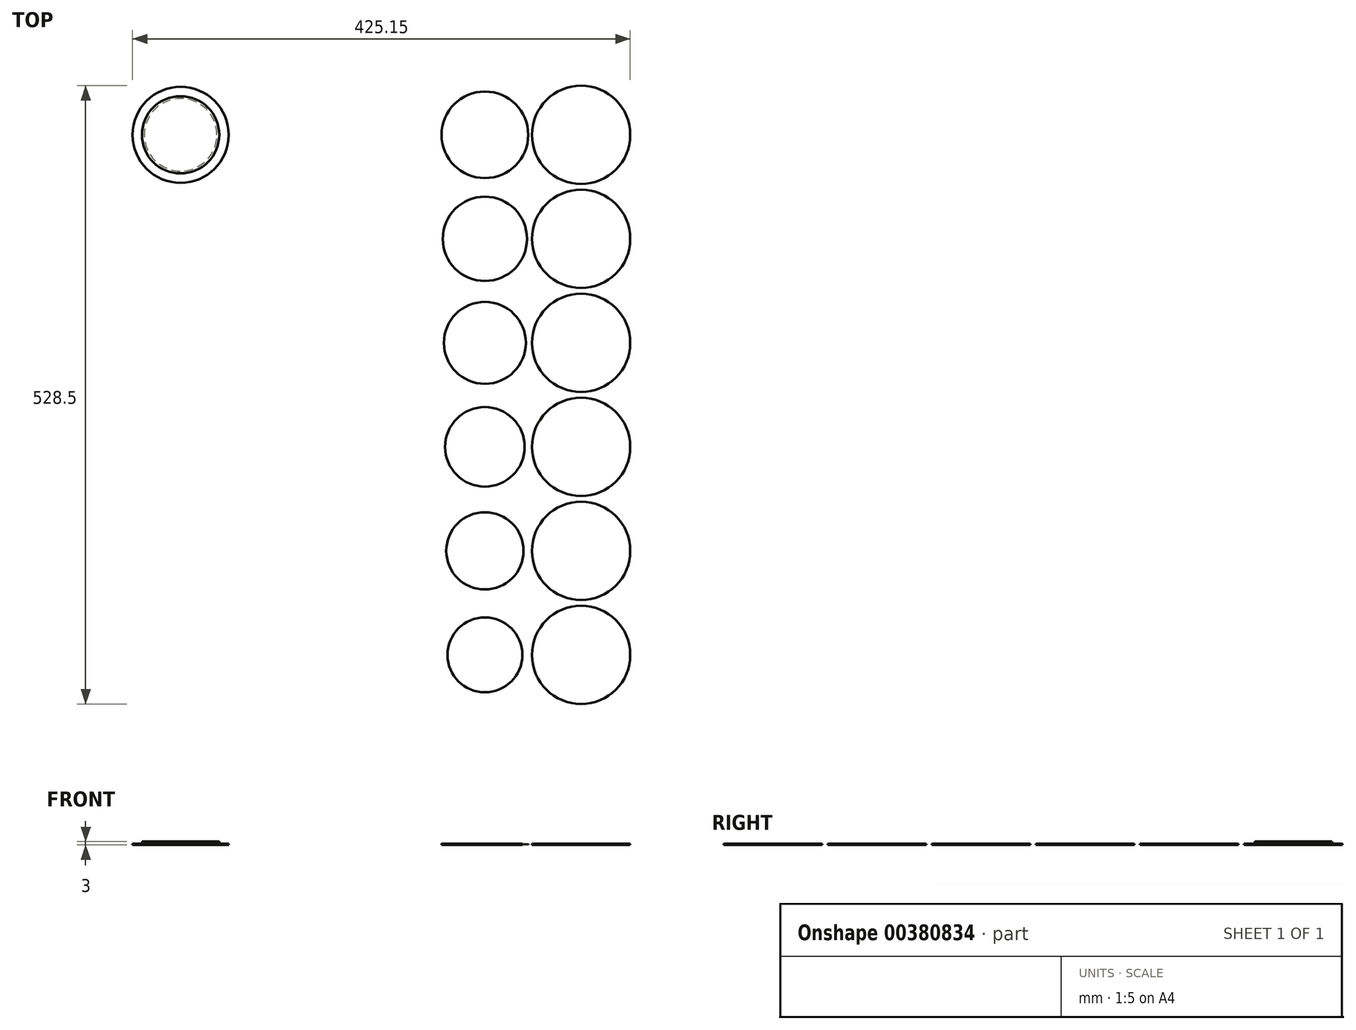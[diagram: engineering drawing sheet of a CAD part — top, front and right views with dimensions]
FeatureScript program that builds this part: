
annotation { "Feature Type Name" : "Feature", "Feature Type Description" : "" }
export const myFeature = defineFeature(function(context is Context, id is Id, definition is map)
    precondition{}
    {
        {
            var Q0;
            Q0=qCreatedBy(makeId("Top.planeOp"),FACE);
            var sketch = newSketch(context, id + "F0", { "sketchPlane" : qUnion([Q0])});
            skArc(sketch, "E0", {"start": v(2.5, -41.93) * mm, "mid": v(0, 42) * mm, "end": v(-2.5, -41.93) * mm});
            skArc(sketch, "E1", {"start": v(2.5, -36.92) * mm, "mid": v(0, 37) * mm, "end": v(-2.5, -36.92) * mm});
            skArc(sketch, "E2", {"start": v(92.4, -41.85) * mm, "mid": v(88.9, 42) * mm, "end": v(85.4, -41.85) * mm});
            skArc(sketch, "E3", {"start": v(92.4, -36.83) * mm, "mid": v(88.9, 37) * mm, "end": v(85.4, -36.83) * mm});
            skArc(sketch, "E4", {"start": v(182.3, -41.76) * mm, "mid": v(177.8, 42) * mm, "end": v(173.3, -41.76) * mm});
            skArc(sketch, "E5", {"start": v(182.3, -36.73) * mm, "mid": v(177.8, 37) * mm, "end": v(173.3, -36.73) * mm});
            skLineSegment(sketch, "E6", {"start": v(0, 0) * mm, "end": v(88.9, 0) * mm, "construction": true});
            skLineSegment(sketch, "E7", {"start": v(88.9, 0) * mm, "end": v(177.8, 0) * mm, "construction": true});
            skLineSegment(sketch, "E8", {"start": v(0, 0) * mm, "end": v(0, -42) * mm, "construction": true});
            skLineSegment(sketch, "E9", {"start": v(-2.5, -36.92) * mm, "end": v(-2.5, -41.93) * mm});
            skLineSegment(sketch, "E10", {"start": v(2.5, -36.92) * mm, "end": v(2.5, -41.93) * mm});
            skLineSegment(sketch, "E11", {"start": v(88.9, 0) * mm, "end": v(88.9, -42) * mm, "construction": true});
            skLineSegment(sketch, "E12", {"start": v(177.8, 0) * mm, "end": v(177.8, -42) * mm, "construction": true});
            skLineSegment(sketch, "E13", {"start": v(85.4, -36.83) * mm, "end": v(85.4, -41.85) * mm});
            skLineSegment(sketch, "E14", {"start": v(92.4, -36.83) * mm, "end": v(92.4, -41.85) * mm});
            skLineSegment(sketch, "E15", {"start": v(173.3, -36.73) * mm, "end": v(173.3, -41.76) * mm});
            skLineSegment(sketch, "E16", {"start": v(182.3, -36.73) * mm, "end": v(182.3, -41.76) * mm});
            skLineSegment(sketch, "E17.0.1.0", {"start": v(0, -88.9) * mm, "end": v(88.9, -88.9) * mm, "construction": true});
            skLineSegment(sketch, "E17.0.1.1", {"start": v(0, -88.9) * mm, "end": v(0, -130.9) * mm, "construction": true});
            skLineSegment(sketch, "E17.0.1.2", {"start": v(88.9, -88.9) * mm, "end": v(88.9, -130.9) * mm, "construction": true});
            skLineSegment(sketch, "E17.0.1.3", {"start": v(88.9, -88.9) * mm, "end": v(177.8, -88.9) * mm, "construction": true});
            skCircle(sketch, "E17.0.1.4", {"center": v(88.9, -88.9) * mm, "radius": 37 * mm, "construction": true});
            skLineSegment(sketch, "E17.0.1.5", {"start": v(177.8, -88.9) * mm, "end": v(177.8, -130.9) * mm, "construction": true});
            skArc(sketch, "E17.0.1.6", {"start": v(92.4, -130.75) * mm, "mid": v(88.9, -46.9) * mm, "end": v(85.4, -130.75) * mm});
            skCircle(sketch, "E17.0.1.7", {"center": v(177.8, -88.9) * mm, "radius": 37 * mm, "construction": true});
            skArc(sketch, "E17.0.1.8", {"start": v(182.3, -130.66) * mm, "mid": v(177.8, -46.9) * mm, "end": v(173.3, -130.66) * mm});
            skCircle(sketch, "E17.0.1.9", {"center": v(0, -88.9) * mm, "radius": 37 * mm, "construction": true});
            skArc(sketch, "E17.0.1.10", {"start": v(2.5, -130.83) * mm, "mid": v(0, -46.9) * mm, "end": v(-2.5, -130.83) * mm});
            skLineSegment(sketch, "E17.0.1.11", {"start": v(92.4, -124.73) * mm, "end": v(92.4, -130.75) * mm});
            skLineSegment(sketch, "E17.0.1.12", {"start": v(85.4, -124.73) * mm, "end": v(85.4, -130.75) * mm});
            skLineSegment(sketch, "E17.0.1.13", {"start": v(2.5, -124.81) * mm, "end": v(2.5, -130.83) * mm});
            skLineSegment(sketch, "E17.0.1.14", {"start": v(173.3, -124.62) * mm, "end": v(173.3, -130.66) * mm});
            skLineSegment(sketch, "E17.0.1.15", {"start": v(182.3, -124.62) * mm, "end": v(182.3, -130.66) * mm});
            skLineSegment(sketch, "E17.0.1.16", {"start": v(-2.5, -125.82) * mm, "end": v(-2.5, -130.83) * mm});
            skLineSegment(sketch, "E17.0.2.0", {"start": v(0, -177.8) * mm, "end": v(88.9, -177.8) * mm, "construction": true});
            skLineSegment(sketch, "E17.0.2.1", {"start": v(0, -177.8) * mm, "end": v(0, -219.8) * mm, "construction": true});
            skLineSegment(sketch, "E17.0.2.2", {"start": v(88.9, -177.8) * mm, "end": v(88.9, -219.8) * mm, "construction": true});
            skLineSegment(sketch, "E17.0.2.3", {"start": v(88.9, -177.8) * mm, "end": v(177.8, -177.8) * mm, "construction": true});
            skCircle(sketch, "E17.0.2.4", {"center": v(88.9, -177.8) * mm, "radius": 37 * mm, "construction": true});
            skLineSegment(sketch, "E17.0.2.5", {"start": v(177.8, -177.8) * mm, "end": v(177.8, -219.8) * mm, "construction": true});
            skArc(sketch, "E17.0.2.6", {"start": v(92.4, -219.65) * mm, "mid": v(88.9, -135.8) * mm, "end": v(85.4, -219.65) * mm});
            skCircle(sketch, "E17.0.2.7", {"center": v(177.8, -177.8) * mm, "radius": 37 * mm, "construction": true});
            skArc(sketch, "E17.0.2.8", {"start": v(182.3, -219.56) * mm, "mid": v(177.8, -135.8) * mm, "end": v(173.3, -219.56) * mm});
            skCircle(sketch, "E17.0.2.9", {"center": v(0, -177.8) * mm, "radius": 37 * mm, "construction": true});
            skArc(sketch, "E17.0.2.10", {"start": v(2.5, -219.73) * mm, "mid": v(0, -135.8) * mm, "end": v(-2.5, -219.73) * mm});
            skLineSegment(sketch, "E17.0.2.11", {"start": v(92.4, -212.62) * mm, "end": v(92.4, -219.65) * mm});
            skLineSegment(sketch, "E17.0.2.12", {"start": v(85.4, -212.62) * mm, "end": v(85.4, -219.65) * mm});
            skLineSegment(sketch, "E17.0.2.13", {"start": v(2.5, -212.71) * mm, "end": v(2.5, -219.73) * mm});
            skLineSegment(sketch, "E17.0.2.14", {"start": v(173.3, -212.5) * mm, "end": v(173.3, -219.56) * mm});
            skLineSegment(sketch, "E17.0.2.15", {"start": v(182.3, -212.5) * mm, "end": v(182.3, -219.56) * mm});
            skLineSegment(sketch, "E17.0.2.16", {"start": v(-2.5, -212.71) * mm, "end": v(-2.5, -219.73) * mm});
            skLineSegment(sketch, "E17.0.3.0", {"start": v(0, -266.7) * mm, "end": v(88.9, -266.7) * mm, "construction": true});
            skLineSegment(sketch, "E17.0.3.1", {"start": v(0, -266.7) * mm, "end": v(0, -308.7) * mm, "construction": true});
            skLineSegment(sketch, "E17.0.3.2", {"start": v(88.9, -266.7) * mm, "end": v(88.9, -308.7) * mm, "construction": true});
            skLineSegment(sketch, "E17.0.3.3", {"start": v(88.9, -266.7) * mm, "end": v(177.8, -266.7) * mm, "construction": true});
            skCircle(sketch, "E17.0.3.4", {"center": v(88.9, -266.7) * mm, "radius": 37 * mm, "construction": true});
            skLineSegment(sketch, "E17.0.3.5", {"start": v(177.8, -266.7) * mm, "end": v(177.8, -308.7) * mm, "construction": true});
            skArc(sketch, "E17.0.3.6", {"start": v(92.4, -308.55) * mm, "mid": v(88.9, -224.7) * mm, "end": v(85.4, -308.55) * mm});
            skCircle(sketch, "E17.0.3.7", {"center": v(177.8, -266.7) * mm, "radius": 37 * mm, "construction": true});
            skArc(sketch, "E17.0.3.8", {"start": v(182.3, -308.46) * mm, "mid": v(177.8, -224.7) * mm, "end": v(173.3, -308.46) * mm});
            skCircle(sketch, "E17.0.3.9", {"center": v(0, -266.7) * mm, "radius": 37 * mm, "construction": true});
            skArc(sketch, "E17.0.3.10", {"start": v(2.5, -308.63) * mm, "mid": v(0, -224.7) * mm, "end": v(-2.5, -308.63) * mm});
            skLineSegment(sketch, "E17.0.3.11", {"start": v(92.4, -300.52) * mm, "end": v(92.4, -308.55) * mm});
            skLineSegment(sketch, "E17.0.3.12", {"start": v(85.4, -300.52) * mm, "end": v(85.4, -308.55) * mm});
            skLineSegment(sketch, "E17.0.3.13", {"start": v(2.5, -300.6) * mm, "end": v(2.5, -308.63) * mm});
            skLineSegment(sketch, "E17.0.3.14", {"start": v(173.3, -300.4) * mm, "end": v(173.3, -308.46) * mm});
            skLineSegment(sketch, "E17.0.3.15", {"start": v(182.3, -300.4) * mm, "end": v(182.3, -308.46) * mm});
            skLineSegment(sketch, "E17.0.3.16", {"start": v(-2.5, -300.6) * mm, "end": v(-2.5, -308.63) * mm});
            skLineSegment(sketch, "E17.0.4.0", {"start": v(0, -355.6) * mm, "end": v(88.9, -355.6) * mm, "construction": true});
            skLineSegment(sketch, "E17.0.4.1", {"start": v(0, -355.6) * mm, "end": v(0, -397.6) * mm, "construction": true});
            skLineSegment(sketch, "E17.0.4.2", {"start": v(88.9, -355.6) * mm, "end": v(88.9, -397.6) * mm, "construction": true});
            skLineSegment(sketch, "E17.0.4.3", {"start": v(88.9, -355.6) * mm, "end": v(177.8, -355.6) * mm, "construction": true});
            skCircle(sketch, "E17.0.4.4", {"center": v(88.9, -355.6) * mm, "radius": 37 * mm, "construction": true});
            skLineSegment(sketch, "E17.0.4.5", {"start": v(177.8, -355.6) * mm, "end": v(177.8, -397.6) * mm, "construction": true});
            skArc(sketch, "E17.0.4.6", {"start": v(92.4, -397.45) * mm, "mid": v(88.9, -313.6) * mm, "end": v(85.4, -397.45) * mm});
            skCircle(sketch, "E17.0.4.7", {"center": v(177.8, -355.6) * mm, "radius": 37 * mm, "construction": true});
            skArc(sketch, "E17.0.4.8", {"start": v(182.3, -397.36) * mm, "mid": v(177.8, -313.6) * mm, "end": v(173.3, -397.36) * mm});
            skCircle(sketch, "E17.0.4.9", {"center": v(0, -355.6) * mm, "radius": 37 * mm, "construction": true});
            skArc(sketch, "E17.0.4.10", {"start": v(2.5, -397.53) * mm, "mid": v(0, -313.6) * mm, "end": v(-2.5, -397.53) * mm});
            skLineSegment(sketch, "E17.0.4.11", {"start": v(92.4, -388.41) * mm, "end": v(92.4, -397.45) * mm});
            skLineSegment(sketch, "E17.0.4.12", {"start": v(85.4, -388.41) * mm, "end": v(85.4, -397.45) * mm});
            skLineSegment(sketch, "E17.0.4.13", {"start": v(2.5, -388.5) * mm, "end": v(2.5, -397.53) * mm});
            skLineSegment(sketch, "E17.0.4.14", {"start": v(173.3, -388.3) * mm, "end": v(173.3, -397.36) * mm});
            skLineSegment(sketch, "E17.0.4.15", {"start": v(182.3, -388.3) * mm, "end": v(182.3, -397.36) * mm});
            skLineSegment(sketch, "E17.0.4.16", {"start": v(-2.5, -388.5) * mm, "end": v(-2.5, -397.53) * mm});
            skLineSegment(sketch, "E17.0.5.0", {"start": v(0, -444.5) * mm, "end": v(88.9, -444.5) * mm, "construction": true});
            skLineSegment(sketch, "E17.0.5.1", {"start": v(0, -444.5) * mm, "end": v(0, -486.5) * mm, "construction": true});
            skLineSegment(sketch, "E17.0.5.2", {"start": v(88.9, -444.5) * mm, "end": v(88.9, -486.5) * mm, "construction": true});
            skLineSegment(sketch, "E17.0.5.3", {"start": v(88.9, -444.5) * mm, "end": v(177.8, -444.5) * mm, "construction": true});
            skCircle(sketch, "E17.0.5.4", {"center": v(88.9, -444.5) * mm, "radius": 37 * mm, "construction": true});
            skLineSegment(sketch, "E17.0.5.5", {"start": v(177.8, -444.5) * mm, "end": v(177.8, -486.5) * mm, "construction": true});
            skArc(sketch, "E17.0.5.6", {"start": v(92.4, -486.35) * mm, "mid": v(88.9, -402.5) * mm, "end": v(85.4, -486.35) * mm});
            skCircle(sketch, "E17.0.5.7", {"center": v(177.8, -444.5) * mm, "radius": 37 * mm, "construction": true});
            skArc(sketch, "E17.0.5.8", {"start": v(182.3, -486.26) * mm, "mid": v(177.8, -402.5) * mm, "end": v(173.3, -486.26) * mm});
            skCircle(sketch, "E17.0.5.9", {"center": v(0, -444.5) * mm, "radius": 37 * mm, "construction": true});
            skArc(sketch, "E17.0.5.10", {"start": v(2.5, -486.43) * mm, "mid": v(0, -402.5) * mm, "end": v(-2.5, -486.43) * mm});
            skLineSegment(sketch, "E17.0.5.11", {"start": v(92.4, -476.3) * mm, "end": v(92.4, -486.35) * mm});
            skLineSegment(sketch, "E17.0.5.12", {"start": v(85.4, -476.3) * mm, "end": v(85.4, -486.35) * mm});
            skLineSegment(sketch, "E17.0.5.13", {"start": v(2.5, -476.4) * mm, "end": v(2.5, -486.43) * mm});
            skLineSegment(sketch, "E17.0.5.14", {"start": v(173.3, -476.18) * mm, "end": v(173.3, -486.26) * mm});
            skLineSegment(sketch, "E17.0.5.15", {"start": v(182.3, -476.18) * mm, "end": v(182.3, -486.26) * mm});
            skLineSegment(sketch, "E17.0.5.16", {"start": v(-2.5, -476.4) * mm, "end": v(-2.5, -486.43) * mm});
            skLineSegment(sketch, "E17.direction1", {"start": v(2.5, -41.93) * mm, "end": v(22.9, -41.93) * mm, "construction": true});
            skLineSegment(sketch, "E17.direction2", {"start": v(-2.5, -41.93) * mm, "end": v(-2.5, -130.83) * mm, "construction": true});
            skArc(sketch, "E18", {"start": v(2.5, -124.81) * mm, "mid": v(0, -52.9) * mm, "end": v(-2.5, -124.81) * mm});
            skArc(sketch, "E19", {"start": v(92.4, -124.73) * mm, "mid": v(88.9, -52.9) * mm, "end": v(85.4, -124.73) * mm});
            skArc(sketch, "E20", {"start": v(182.3, -124.62) * mm, "mid": v(177.8, -52.9) * mm, "end": v(173.3, -124.62) * mm});
            skArc(sketch, "E21", {"start": v(182.3, -212.5) * mm, "mid": v(177.8, -142.8) * mm, "end": v(173.3, -212.5) * mm});
            skArc(sketch, "E22", {"start": v(92.4, -212.62) * mm, "mid": v(88.9, -142.8) * mm, "end": v(85.4, -212.62) * mm});
            skArc(sketch, "E23", {"start": v(2.5, -212.71) * mm, "mid": v(0, -142.8) * mm, "end": v(-2.5, -212.71) * mm});
            skArc(sketch, "E24", {"start": v(2.5, -300.6) * mm, "mid": v(0, -232.7) * mm, "end": v(-2.5, -300.6) * mm});
            skArc(sketch, "E25", {"start": v(92.4, -300.52) * mm, "mid": v(88.9, -232.7) * mm, "end": v(85.4, -300.52) * mm});
            skArc(sketch, "E26", {"start": v(182.3, -300.4) * mm, "mid": v(177.8, -232.7) * mm, "end": v(173.3, -300.4) * mm});
            skArc(sketch, "E27", {"start": v(182.3, -388.3) * mm, "mid": v(177.8, -322.6) * mm, "end": v(173.3, -388.3) * mm});
            skArc(sketch, "E28", {"start": v(92.4, -388.41) * mm, "mid": v(88.9, -322.6) * mm, "end": v(85.4, -388.41) * mm});
            skArc(sketch, "E29", {"start": v(2.5, -388.5) * mm, "mid": v(0, -322.6) * mm, "end": v(-2.5, -388.5) * mm});
            skArc(sketch, "E30", {"start": v(2.5, -476.4) * mm, "mid": v(0, -412.5) * mm, "end": v(-2.5, -476.4) * mm});
            skArc(sketch, "E31", {"start": v(92.4, -476.3) * mm, "mid": v(88.9, -412.5) * mm, "end": v(85.4, -476.3) * mm});
            skArc(sketch, "E32", {"start": v(182.3, -476.18) * mm, "mid": v(177.8, -412.5) * mm, "end": v(173.3, -476.18) * mm});
            skPoint(sketch, "E33.orphan", {"position": v(2.5, -125.82) * mm});
            skLineSegment(sketch, "E34", {"start": v(-2.5, -125.82) * mm, "end": v(-2.5, -124.81) * mm});
            skPoint(sketch, "E35.orphan", {"position": v(85.4, -125.73) * mm});
            skPoint(sketch, "E36.orphan", {"position": v(92.4, -125.73) * mm});
            skPoint(sketch, "E37.orphan", {"position": v(173.3, -125.63) * mm});
            skPoint(sketch, "E38.orphan", {"position": v(182.3, -125.63) * mm});
            skPoint(sketch, "E39.orphan", {"position": v(-2.5, -214.72) * mm});
            skPoint(sketch, "E40.orphan", {"position": v(2.5, -214.72) * mm});
            skPoint(sketch, "E41.orphan", {"position": v(85.4, -214.63) * mm});
            skPoint(sketch, "E42.orphan", {"position": v(92.4, -214.63) * mm});
            skPoint(sketch, "E43.orphan", {"position": v(173.3, -214.53) * mm});
            skPoint(sketch, "E44.orphan", {"position": v(182.3, -214.53) * mm});
            skPoint(sketch, "E45.orphan", {"position": v(182.3, -303.43) * mm});
            skPoint(sketch, "E46.orphan", {"position": v(173.3, -303.43) * mm});
            skPoint(sketch, "E47.orphan", {"position": v(92.4, -303.53) * mm});
            skPoint(sketch, "E48.orphan", {"position": v(85.4, -303.53) * mm});
            skPoint(sketch, "E49.orphan", {"position": v(-2.5, -303.62) * mm});
            skPoint(sketch, "E50.orphan", {"position": v(2.5, -303.62) * mm});
            skPoint(sketch, "E51.orphan", {"position": v(-2.5, -392.52) * mm});
            skPoint(sketch, "E52.orphan", {"position": v(2.5, -392.52) * mm});
            skPoint(sketch, "E53.orphan", {"position": v(85.4, -392.43) * mm});
            skPoint(sketch, "E54.orphan", {"position": v(92.4, -392.43) * mm});
            skPoint(sketch, "E55.orphan", {"position": v(182.3, -392.33) * mm});
            skPoint(sketch, "E56.orphan", {"position": v(173.3, -392.33) * mm});
            skPoint(sketch, "E57.orphan", {"position": v(-2.5, -481.42) * mm});
            skPoint(sketch, "E58.orphan", {"position": v(2.5, -481.42) * mm});
            skPoint(sketch, "E59.orphan", {"position": v(85.4, -481.33) * mm});
            skPoint(sketch, "E60.orphan", {"position": v(92.4, -481.33) * mm});
            skPoint(sketch, "E61.orphan", {"position": v(173.3, -481.23) * mm});
            skPoint(sketch, "E62.orphan", {"position": v(182.3, -481.23) * mm});
            skSolve(sketch);
        }
        {
            var Q0;
            Q0=qSketchRegion(id+"F0",true);
            extrude(context, id + "F1", {"entities" : qUnion([Q0]), "depth" : 1 * mm});
        }
        {
            var Q0;
            Q0=qCreatedBy(makeId("Top.planeOp"),FACE);
            var sketch = newSketch(context, id + "F2", { "sketchPlane" : qUnion([Q0])});
            skCircle(sketch, "E63", {"center": v(259.98, 0) * mm, "radius": 37 * mm});
            skCircle(sketch, "E64", {"center": v(342.15, 0) * mm, "radius": 42 * mm});
            skCircle(sketch, "E65.0.1.0", {"center": v(342.15, -88.9) * mm, "radius": 42 * mm});
            skCircle(sketch, "E65.0.2.0", {"center": v(342.15, -177.8) * mm, "radius": 42 * mm});
            skCircle(sketch, "E65.0.3.0", {"center": v(342.15, -266.7) * mm, "radius": 42 * mm});
            skCircle(sketch, "E65.0.4.0", {"center": v(342.15, -355.6) * mm, "radius": 42 * mm});
            skCircle(sketch, "E65.0.5.0", {"center": v(342.15, -444.5) * mm, "radius": 42 * mm});
            skLineSegment(sketch, "E65.direction1", {"start": v(342.15, 0) * mm, "end": v(367.55, 0) * mm, "construction": true});
            skLineSegment(sketch, "E65.direction2", {"start": v(342.15, 0) * mm, "end": v(342.15, -88.9) * mm, "construction": true});
            skCircle(sketch, "E66", {"center": v(259.98, -88.9) * mm, "radius": 36 * mm});
            skCircle(sketch, "E67", {"center": v(259.98, -177.8) * mm, "radius": 35 * mm});
            skCircle(sketch, "E68", {"center": v(259.98, -266.7) * mm, "radius": 34 * mm});
            skCircle(sketch, "E69", {"center": v(259.98, -355.6) * mm, "radius": 33 * mm});
            skCircle(sketch, "E70", {"center": v(259.98, -444.5) * mm, "radius": 32 * mm});
            skSolve(sketch);
        }
        {
            var Q0;
            Q0=qSketchRegion(id+"F2",true);
            extrude(context, id + "F3", {"entities" : qUnion([Q0]), "depth" : 1 * mm});
        }
        {
            var Q0;
            Q0=qCreatedBy(makeId("Top.planeOp"),FACE);
            var sketch = newSketch(context, id + "F4", { "sketchPlane" : qUnion([Q0])});
            skCircle(sketch, "E71", {"center": v(-89.46, 0) * mm, "radius": 42 * mm});
            skCircle(sketch, "E72", {"center": v(-89.46, 0) * mm, "radius": 37 * mm});
            skCircle(sketch, "E73.0.1.0", {"center": v(-89.46, -88.9) * mm, "radius": 42 * mm});
            skCircle(sketch, "E73.0.2.0", {"center": v(-89.46, -177.8) * mm, "radius": 42 * mm});
            skCircle(sketch, "E73.0.3.0", {"center": v(-89.46, -266.7) * mm, "radius": 42 * mm});
            skCircle(sketch, "E73.0.4.0", {"center": v(-89.46, -355.6) * mm, "radius": 42 * mm});
            skCircle(sketch, "E73.0.5.0", {"center": v(-89.46, -444.5) * mm, "radius": 42 * mm});
            skLineSegment(sketch, "E73.direction1", {"start": v(-89.46, 0) * mm, "end": v(-64.06, 0) * mm, "construction": true});
            skLineSegment(sketch, "E73.direction2", {"start": v(-89.46, 0) * mm, "end": v(-89.46, -88.9) * mm, "construction": true});
            skCircle(sketch, "E74", {"center": v(-89.46, -88.9) * mm, "radius": 36 * mm});
            skCircle(sketch, "E75", {"center": v(-89.46, -177.8) * mm, "radius": 35 * mm});
            skCircle(sketch, "E76", {"center": v(-89.46, -266.7) * mm, "radius": 34 * mm});
            skCircle(sketch, "E77", {"center": v(-89.46, -355.6) * mm, "radius": 33 * mm});
            skCircle(sketch, "E78", {"center": v(-89.46, -444.5) * mm, "radius": 32 * mm});
            skSolve(sketch);
        }
        {
            var Q0;
            Q0=qSketchRegion(id+"F4",true);
            extrude(context, id + "F5", {"entities" : qUnion([Q0]), "depth" : 1 * mm});
        }
        {
            var Q0;
            Q0=makeQuery(id+"F5.opExtrude","SWEPT_BODY",BODY,{"disambiguationData":[OSD([sQuery(id+"F4.wireOp",EDGE,"E73.0.5.0"),sQuery(id+"F4.wireOp",EDGE,"E78")])]});
            var Q1;
            Q1=makeQuery(id+"F5.opExtrude","SWEPT_BODY",BODY,{"disambiguationData":[OSD([sQuery(id+"F4.wireOp",EDGE,"E73.0.4.0"),sQuery(id+"F4.wireOp",EDGE,"E77")])]});
            var Q2;
            Q2=makeQuery(id+"F5.opExtrude","SWEPT_BODY",BODY,{"disambiguationData":[OSD([sQuery(id+"F4.wireOp",EDGE,"E73.0.3.0"),sQuery(id+"F4.wireOp",EDGE,"E76")])]});
            var Q3;
            Q3=makeQuery(id+"F5.opExtrude","SWEPT_BODY",BODY,{"disambiguationData":[OSD([sQuery(id+"F4.wireOp",EDGE,"E73.0.2.0"),sQuery(id+"F4.wireOp",EDGE,"E75")])]});
            var Q4;
            Q4=makeQuery(id+"F5.opExtrude","SWEPT_BODY",BODY,{"disambiguationData":[OSD([sQuery(id+"F4.wireOp",EDGE,"E73.0.1.0"),sQuery(id+"F4.wireOp",EDGE,"E74")])]});
            var Q5;
            Q5=makeQuery(id+"F5.opExtrude","SWEPT_BODY",BODY,{"disambiguationData":[OSD([sQuery(id+"F4.wireOp",EDGE,"E71"),sQuery(id+"F4.wireOp",EDGE,"E72")])]});
            var Q6;
            Q6=makeQuery(id+"F1.opExtrude","SWEPT_BODY",BODY,{"disambiguationData":[OSD([sQuery(id+"F0.wireOp",EDGE,"E17.0.5.10"),sQuery(id+"F0.wireOp",EDGE,"E17.0.5.13"),sQuery(id+"F0.wireOp",EDGE,"E17.0.5.16"),sQuery(id+"F0.wireOp",EDGE,"E30")])]});
            var Q7;
            Q7=makeQuery(id+"F1.opExtrude","SWEPT_BODY",BODY,{"disambiguationData":[OSD([sQuery(id+"F0.wireOp",EDGE,"E17.0.5.8"),sQuery(id+"F0.wireOp",EDGE,"E17.0.5.14"),sQuery(id+"F0.wireOp",EDGE,"E17.0.5.15"),sQuery(id+"F0.wireOp",EDGE,"E32")])]});
            var Q8;
            Q8=makeQuery(id+"F1.opExtrude","SWEPT_BODY",BODY,{"disambiguationData":[OSD([sQuery(id+"F0.wireOp",EDGE,"E17.0.5.6"),sQuery(id+"F0.wireOp",EDGE,"E17.0.5.11"),sQuery(id+"F0.wireOp",EDGE,"E17.0.5.12"),sQuery(id+"F0.wireOp",EDGE,"E31")])]});
            var Q9;
            Q9=makeQuery(id+"F1.opExtrude","SWEPT_BODY",BODY,{"disambiguationData":[OSD([sQuery(id+"F0.wireOp",EDGE,"E17.0.4.10"),sQuery(id+"F0.wireOp",EDGE,"E17.0.4.13"),sQuery(id+"F0.wireOp",EDGE,"E17.0.4.16"),sQuery(id+"F0.wireOp",EDGE,"E29")])]});
            var Q10;
            Q10=makeQuery(id+"F1.opExtrude","SWEPT_BODY",BODY,{"disambiguationData":[OSD([sQuery(id+"F0.wireOp",EDGE,"E17.0.4.8"),sQuery(id+"F0.wireOp",EDGE,"E17.0.4.14"),sQuery(id+"F0.wireOp",EDGE,"E17.0.4.15"),sQuery(id+"F0.wireOp",EDGE,"E27")])]});
            var Q11;
            Q11=makeQuery(id+"F1.opExtrude","SWEPT_BODY",BODY,{"disambiguationData":[OSD([sQuery(id+"F0.wireOp",EDGE,"E17.0.4.6"),sQuery(id+"F0.wireOp",EDGE,"E17.0.4.11"),sQuery(id+"F0.wireOp",EDGE,"E17.0.4.12"),sQuery(id+"F0.wireOp",EDGE,"E28")])]});
            var Q12;
            Q12=makeQuery(id+"F1.opExtrude","SWEPT_BODY",BODY,{"disambiguationData":[OSD([sQuery(id+"F0.wireOp",EDGE,"E17.0.3.10"),sQuery(id+"F0.wireOp",EDGE,"E17.0.3.13"),sQuery(id+"F0.wireOp",EDGE,"E17.0.3.16"),sQuery(id+"F0.wireOp",EDGE,"E24")])]});
            var Q13;
            Q13=makeQuery(id+"F1.opExtrude","SWEPT_BODY",BODY,{"disambiguationData":[OSD([sQuery(id+"F0.wireOp",EDGE,"E17.0.3.8"),sQuery(id+"F0.wireOp",EDGE,"E17.0.3.14"),sQuery(id+"F0.wireOp",EDGE,"E17.0.3.15"),sQuery(id+"F0.wireOp",EDGE,"E26")])]});
            var Q14;
            Q14=makeQuery(id+"F1.opExtrude","SWEPT_BODY",BODY,{"disambiguationData":[OSD([sQuery(id+"F0.wireOp",EDGE,"E17.0.3.6"),sQuery(id+"F0.wireOp",EDGE,"E17.0.3.11"),sQuery(id+"F0.wireOp",EDGE,"E17.0.3.12"),sQuery(id+"F0.wireOp",EDGE,"E25")])]});
            var Q15;
            Q15=makeQuery(id+"F1.opExtrude","SWEPT_BODY",BODY,{"disambiguationData":[OSD([sQuery(id+"F0.wireOp",EDGE,"E17.0.2.10"),sQuery(id+"F0.wireOp",EDGE,"E17.0.2.13"),sQuery(id+"F0.wireOp",EDGE,"E17.0.2.16"),sQuery(id+"F0.wireOp",EDGE,"E23")])]});
            var Q16;
            Q16=makeQuery(id+"F1.opExtrude","SWEPT_BODY",BODY,{"disambiguationData":[OSD([sQuery(id+"F0.wireOp",EDGE,"E17.0.2.8"),sQuery(id+"F0.wireOp",EDGE,"E17.0.2.14"),sQuery(id+"F0.wireOp",EDGE,"E17.0.2.15"),sQuery(id+"F0.wireOp",EDGE,"E21")])]});
            var Q17;
            Q17=makeQuery(id+"F1.opExtrude","SWEPT_BODY",BODY,{"disambiguationData":[OSD([sQuery(id+"F0.wireOp",EDGE,"E17.0.2.6"),sQuery(id+"F0.wireOp",EDGE,"E17.0.2.11"),sQuery(id+"F0.wireOp",EDGE,"E17.0.2.12"),sQuery(id+"F0.wireOp",EDGE,"E22")])]});
            var Q18;
            Q18=makeQuery(id+"F1.opExtrude","SWEPT_BODY",BODY,{"disambiguationData":[OSD([sQuery(id+"F0.wireOp",EDGE,"E17.0.1.10"),sQuery(id+"F0.wireOp",EDGE,"E17.0.1.13"),sQuery(id+"F0.wireOp",EDGE,"E17.0.1.16"),sQuery(id+"F0.wireOp",EDGE,"E18"),sQuery(id+"F0.wireOp",EDGE,"E34")])]});
            var Q19;
            Q19=makeQuery(id+"F1.opExtrude","SWEPT_BODY",BODY,{"disambiguationData":[OSD([sQuery(id+"F0.wireOp",EDGE,"E17.0.1.8"),sQuery(id+"F0.wireOp",EDGE,"E17.0.1.14"),sQuery(id+"F0.wireOp",EDGE,"E17.0.1.15"),sQuery(id+"F0.wireOp",EDGE,"E20")])]});
            var Q20;
            Q20=makeQuery(id+"F1.opExtrude","SWEPT_BODY",BODY,{"disambiguationData":[OSD([sQuery(id+"F0.wireOp",EDGE,"E17.0.1.6"),sQuery(id+"F0.wireOp",EDGE,"E17.0.1.11"),sQuery(id+"F0.wireOp",EDGE,"E17.0.1.12"),sQuery(id+"F0.wireOp",EDGE,"E19")])]});
            var Q21;
            Q21=makeQuery(id+"F1.opExtrude","SWEPT_BODY",BODY,{"disambiguationData":[OSD([sQuery(id+"F0.wireOp",EDGE,"E4"),sQuery(id+"F0.wireOp",EDGE,"E5"),sQuery(id+"F0.wireOp",EDGE,"E15"),sQuery(id+"F0.wireOp",EDGE,"E16")])]});
            var Q22;
            Q22=makeQuery(id+"F1.opExtrude","SWEPT_BODY",BODY,{"disambiguationData":[OSD([sQuery(id+"F0.wireOp",EDGE,"E2"),sQuery(id+"F0.wireOp",EDGE,"E3"),sQuery(id+"F0.wireOp",EDGE,"E13"),sQuery(id+"F0.wireOp",EDGE,"E14")])]});
            var Q23;
            Q23=makeQuery(id+"F1.opExtrude","SWEPT_BODY",BODY,{"disambiguationData":[OSD([sQuery(id+"F0.wireOp",EDGE,"E0"),sQuery(id+"F0.wireOp",EDGE,"E1"),sQuery(id+"F0.wireOp",EDGE,"E9"),sQuery(id+"F0.wireOp",EDGE,"E10")])]});
            deleteBodies(context, id + "F6", {"entities" : qUnion([Q0, Q1, Q2, Q3, Q4, Q5, Q6, Q7, Q8, Q9, Q10, Q11, Q12, Q13, Q14, Q15, Q16, Q17, Q18, Q19, Q20, Q21, Q22, Q23])});
        }
        {
            var Q0;
            Q0=qCreatedBy(makeId("Top.planeOp"),FACE);
            var sketch = newSketch(context, id + "F7", { "sketchPlane" : qUnion([Q0])});
            skCircle(sketch, "E79", {"center": v(0, 0) * mm, "radius": 41 * mm});
            skCircle(sketch, "E80", {"center": v(0, 0) * mm, "radius": 33 * mm});
            skCircle(sketch, "E81", {"center": v(0, 0) * mm, "radius": 31 * mm});
            skSolve(sketch);
        }
        {
            var Q0;
            Q0=makeQuery(id+"F7.imprint","IMPRINT",FACE,{"disambiguationData":[TD([[makeQuery(id+"F7.imprint","IMPRINT",EDGE,{"derivedFrom":sQuery(id+"F7.wireOp",EDGE,"E79")}),1.0]])]});
            var Q1;
            Q1=makeQuery(id+"F7.imprint","IMPRINT",FACE,{"disambiguationData":[TD([[makeQuery(id+"F7.imprint","IMPRINT",EDGE,{"derivedFrom":sQuery(id+"F7.wireOp",EDGE,"E81")}),1.0]])]});
            var Q2;
            Q2=makeQuery(id+"F7.imprint","IMPRINT",FACE,{"disambiguationData":[TD([[makeQuery(id+"F7.imprint","IMPRINT",EDGE,{"derivedFrom":sQuery(id+"F7.wireOp",EDGE,"E80")}),1.0]])]});
            extrude(context, id + "F8", {"entities" : qUnion([Q0, Q1, Q2]), "depth" : 1 * mm});
        }
        {
            var Q0;
            Q0=makeQuery(id+"F7.imprint","IMPRINT",FACE,{"disambiguationData":[TD([[makeQuery(id+"F7.imprint","IMPRINT",EDGE,{"derivedFrom":sQuery(id+"F7.wireOp",EDGE,"E81")}),1.0]])]});
            extrude(context, id + "F9", {"entities" : qUnion([Q0]), "operationType" : NewBodyOperationType.ADD, "depth" : 2 * mm});
        }
        {
            var Q0;
            Q0=makeQuery(id+"F9.opExtrude","CAP_FACE",FACE,{"disambiguationData":[OSD([sQuery(id+"F7.wireOp",EDGE,"E81")])],"isStart":false});
            var sketch = newSketch(context, id + "F10", { "sketchPlane" : qUnion([Q0])});
            skCircle(sketch, "E82.0", {"center": v(0, 0) * mm, "radius": 33 * mm});
            skSolve(sketch);
        }
        {
            var Q0;
            Q0 = qSketchRegion(id + "F10", true);
            extrude(context, id + "F11", {"entities" : qUnion([Q0]), "operationType" : NewBodyOperationType.ADD, "depth" : 1 * mm});
        }
    });
